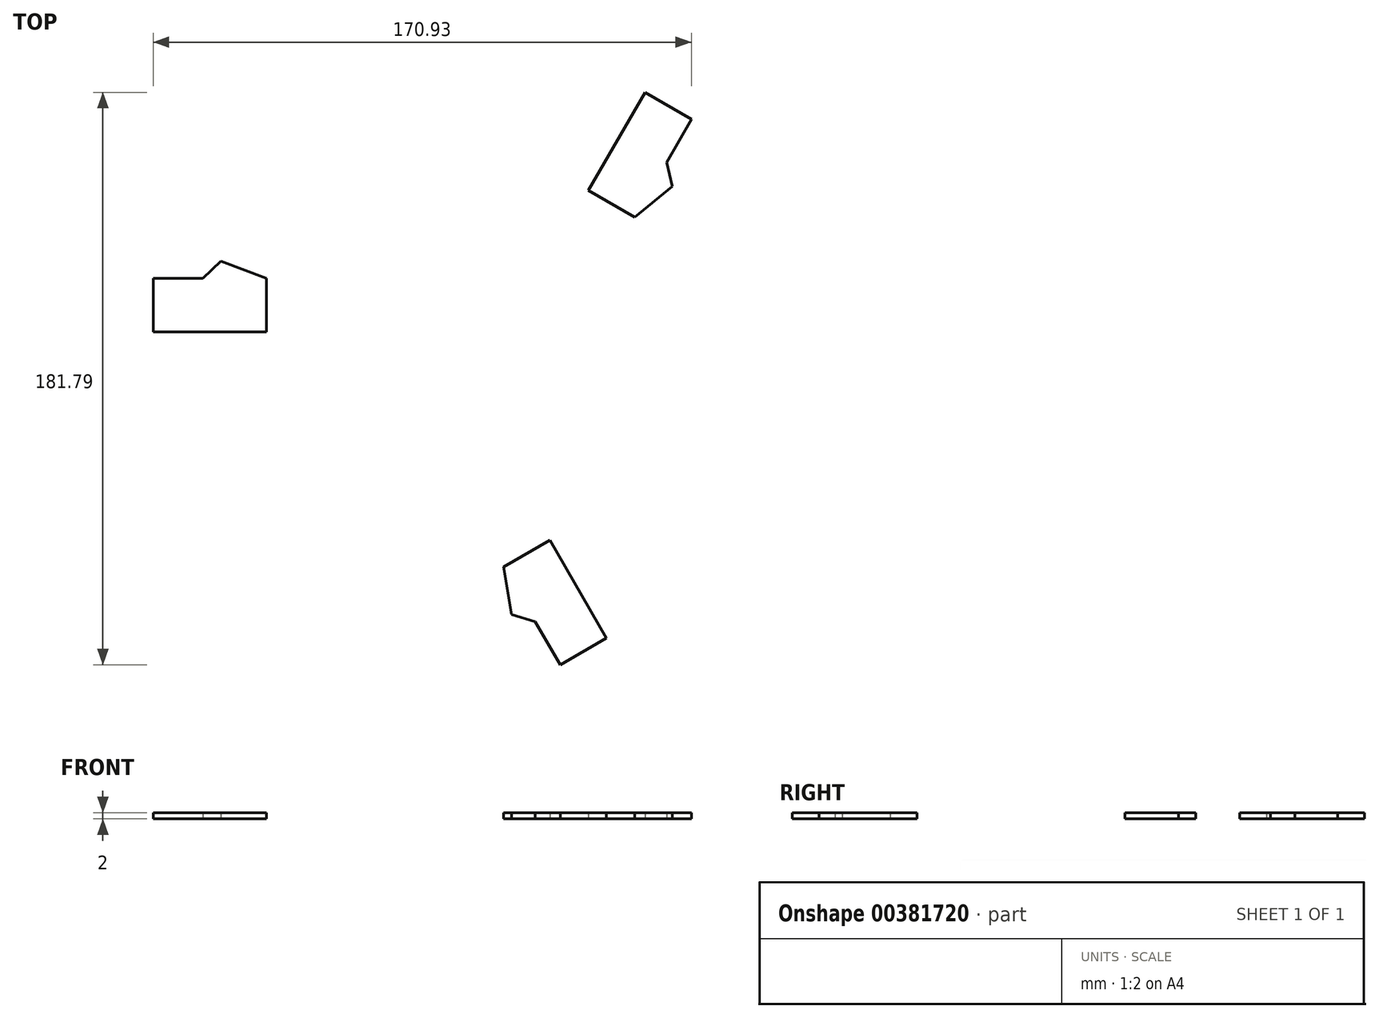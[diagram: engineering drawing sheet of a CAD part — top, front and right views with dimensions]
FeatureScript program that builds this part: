
annotation { "Feature Type Name" : "Feature", "Feature Type Description" : "" }
export const myFeature = defineFeature(function(context is Context, id is Id, definition is map)
    precondition{}
    {
        {
            var Q0;
            Q0=qCreatedBy(makeId("Top.planeOp"),FACE);
            var sketch = newSketch(context, id + "F0", { "sketchPlane" : qUnion([Q0])});
            skLineSegment(sketch, "E0", {"start": v(-100.06, 24.06) * mm, "end": v(-84.27, 24.06) * mm});
            skLineSegment(sketch, "E1", {"start": v(-84.27, 24.06) * mm, "end": v(-78.56, 29.51) * mm});
            skLineSegment(sketch, "E2", {"start": v(-78.56, 29.51) * mm, "end": v(-64.12, 24.06) * mm});
            skLineSegment(sketch, "E3", {"start": v(-64.12, 24.06) * mm, "end": v(-64.12, 7.08) * mm});
            skLineSegment(sketch, "E4", {"start": v(-64.12, 7.08) * mm, "end": v(-100.06, 7.08) * mm});
            skLineSegment(sketch, "E5", {"start": v(-100.06, 7.08) * mm, "end": v(-100.06, 24.06) * mm});
            skLineSegment(sketch, "E6.1.0", {"start": v(25.93, -59.07) * mm, "end": v(43.9, -90.2) * mm});
            skLineSegment(sketch, "E6.1.1", {"start": v(43.9, -90.2) * mm, "end": v(29.2, -98.68) * mm});
            skLineSegment(sketch, "E6.1.2", {"start": v(29.2, -98.68) * mm, "end": v(21.3, -85) * mm});
            skLineSegment(sketch, "E6.1.3", {"start": v(21.3, -85) * mm, "end": v(13.72, -82.79) * mm});
            skLineSegment(sketch, "E6.1.4", {"start": v(13.72, -82.79) * mm, "end": v(11.22, -67.56) * mm});
            skLineSegment(sketch, "E6.1.5", {"start": v(11.22, -67.56) * mm, "end": v(25.93, -59.07) * mm});
            skLineSegment(sketch, "E6.2.0", {"start": v(38.2, 52) * mm, "end": v(56.16, 83.11) * mm});
            skLineSegment(sketch, "E6.2.1", {"start": v(56.16, 83.11) * mm, "end": v(70.87, 74.62) * mm});
            skLineSegment(sketch, "E6.2.2", {"start": v(70.87, 74.62) * mm, "end": v(62.97, 60.94) * mm});
            skLineSegment(sketch, "E6.2.3", {"start": v(62.97, 60.94) * mm, "end": v(64.84, 53.28) * mm});
            skLineSegment(sketch, "E6.2.4", {"start": v(64.84, 53.28) * mm, "end": v(52.9, 43.5) * mm});
            skLineSegment(sketch, "E6.2.5", {"start": v(52.9, 43.5) * mm, "end": v(38.2, 52) * mm});
            skPoint(sketch, "E6.center", {"position": v(0, 0) * mm});
            skLineSegment(sketch, "E7.1.0", {"start": v(-53.74, 87.77) * mm, "end": v(-42.57, 76.6) * mm});
            skLineSegment(sketch, "E7.1.1", {"start": v(-65.74, 75.76) * mm, "end": v(-53.74, 87.77) * mm});
            skLineSegment(sketch, "E7.1.2", {"start": v(-40.34, 50.35) * mm, "end": v(-65.74, 75.76) * mm});
            skLineSegment(sketch, "E7.2.0", {"start": v(24.06, 100.06) * mm, "end": v(24.06, 84.27) * mm});
            skLineSegment(sketch, "E7.2.1", {"start": v(7.08, 100.06) * mm, "end": v(24.06, 100.06) * mm});
            skLineSegment(sketch, "E7.2.2", {"start": v(7.08, 64.12) * mm, "end": v(7.08, 100.06) * mm});
            skLineSegment(sketch, "E7.anchor1", {"start": v(0, 0) * mm, "end": v(-100.06, 7.08) * mm, "construction": true});
            skLineSegment(sketch, "E7.anchor2", {"start": v(0, 0) * mm, "end": v(7.08, 100.06) * mm, "construction": true});
            skSolve(sketch);
        }
        {
            var Q0;
            Q0 = qSketchRegion(id + "F0", true);
            extrude(context, id + "F1", {"entities" : qUnion([Q0]), "depth" : 2 * mm, "offsetDistance" : 25 * mm});
        }
    });
